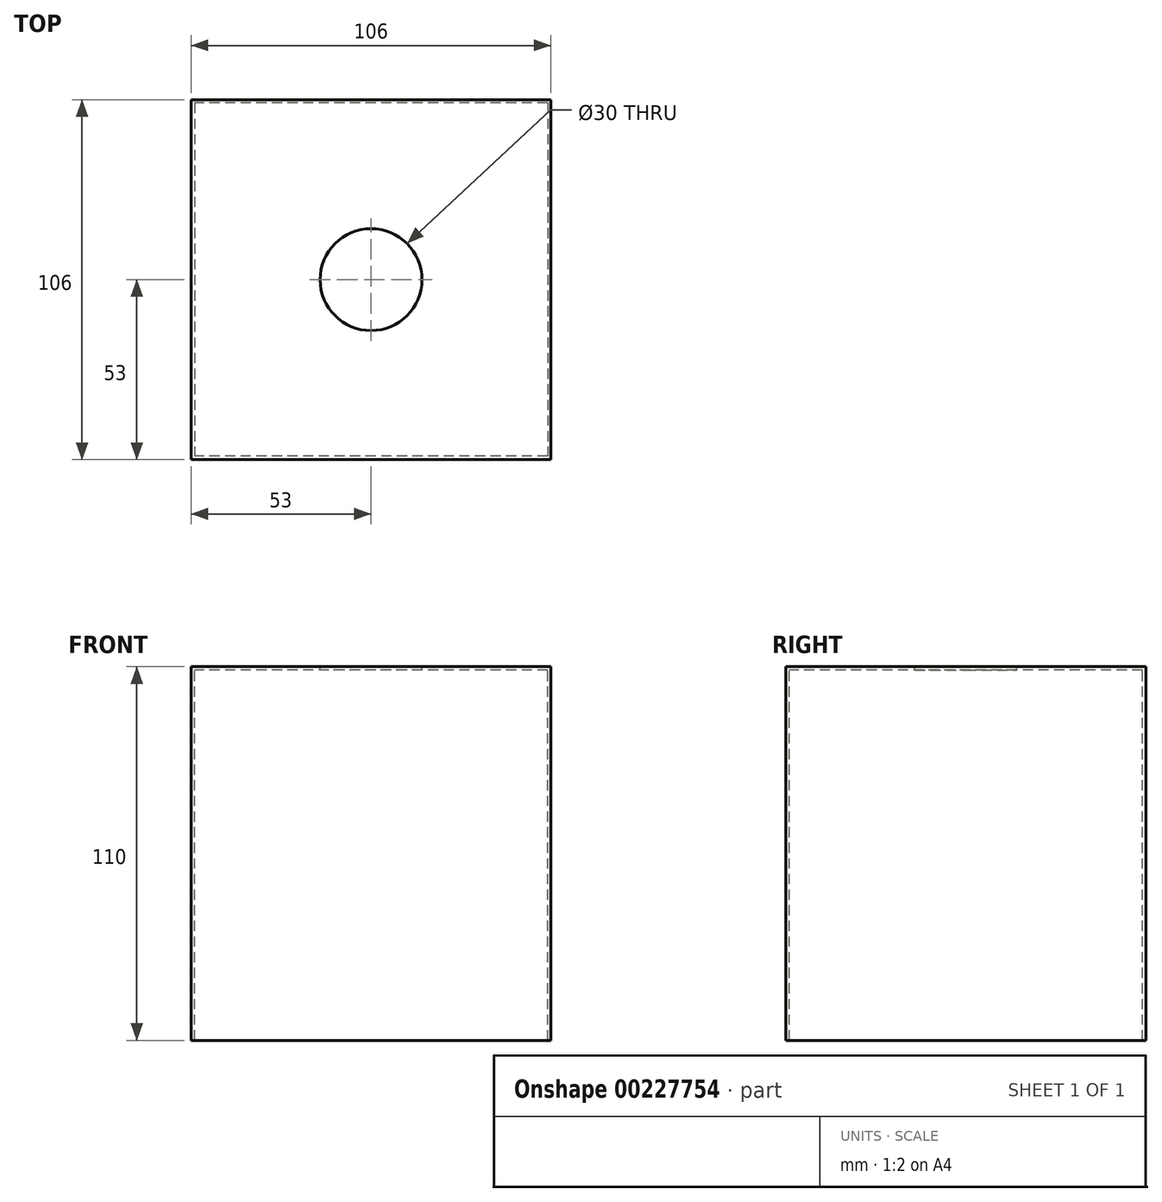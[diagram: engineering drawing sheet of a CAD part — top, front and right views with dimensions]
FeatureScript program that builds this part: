
annotation { "Feature Type Name" : "Feature", "Feature Type Description" : "" }
export const myFeature = defineFeature(function(context is Context, id is Id, definition is map)
    precondition{}
    {
        {
            var Q0;
            Q0=qCreatedBy(makeId("Top.planeOp"),FACE);
            var sketch = newSketch(context, id + "F0", { "sketchPlane" : qUnion([Q0])});
            skLineSegment(sketch, "E0.bottom", {"start": v(53, 53) * mm, "end": v(-53, 53) * mm});
            skLineSegment(sketch, "E0.top", {"start": v(53, -53) * mm, "end": v(-53, -53) * mm});
            skLineSegment(sketch, "E0.left", {"start": v(53, 53) * mm, "end": v(53, -53) * mm});
            skLineSegment(sketch, "E0.right", {"start": v(-53, 53) * mm, "end": v(-53, -53) * mm});
            skPoint(sketch, "E0.middle", {"position": v(0, 0) * mm});
            skCircle(sketch, "E1", {"center": v(0, 0) * mm, "radius": 15 * mm});
            skCircle(sketch, "E2", {"center": v(0, 0) * mm, "radius": 10 * mm});
            skSolve(sketch);
        }
        {
            var Q0;
            Q0=makeQuery(id+"F0.imprint","IMPRINT",FACE,{"disambiguationData":[TD([[makeQuery(id+"F0.imprint","IMPRINT",EDGE,{"derivedFrom":sQuery(id+"F0.wireOp",EDGE,"E0.bottom")}),1.0]])]});
            extrude(context, id + "F1", {"entities" : qUnion([Q0]), "oppositeDirection" : true, "depth" : 110 * mm});
        }
        {
            var Q0;
            Q0=makeQuery(id+"F1.opExtrude","CAP_FACE",FACE,{"disambiguationData":[OSD([sQuery(id+"F0.wireOp",EDGE,"E0.bottom"),sQuery(id+"F0.wireOp",EDGE,"E0.top"),sQuery(id+"F0.wireOp",EDGE,"E0.left"),sQuery(id+"F0.wireOp",EDGE,"E0.right")])],"isStart":false});
            var Q1;
            Q1=makeQuery(id+"F1.opExtrude","SWEPT_FACE",FACE,{"disambiguationData":[OSD([sQuery(id+"F0.wireOp",EDGE,"E1")])]});
            shell(context, id + "F2", {"entities" : qUnion([Q0, Q1]), "thickness" : 1 * mm});
        }
    });
